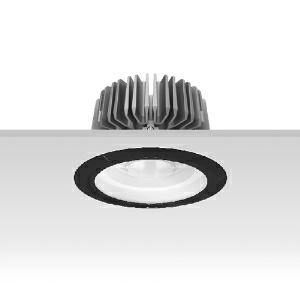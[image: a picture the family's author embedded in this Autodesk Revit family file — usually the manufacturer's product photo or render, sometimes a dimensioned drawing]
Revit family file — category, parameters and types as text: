
# Revit family: 3f_filippi_-_3f_reno_bianco_ampio_3f_filippi_-_30387_a01024_-_3f_reno_150_wh_3000-930_dali_wide___vt_bk_413a
name_source: partatom
category: Lighting Fixtures
units: mm (PartAtom-declared; Revit-internal decimal feet)

## family parameters
Cut with Voids When Loaded = No
Host = Face
Light Source = No
Part Type = Normal
Room Calculation Point = No
Round Connector Dimension = Use Diameter
Shared = No

## types (1)
- 3F Filippi - 3F Reno Bianco Ampio (1 x LED, 2656 lm, 37 W, 3000 K)
    Apparent Load = 37 VA
    Approval mark = CE
    CIE Flux Codes = 74 93 99 100 100
    Color Rendering = 90
    Color Temperature = 3000 K
    Control Gear = Electronic transformer
    Default Elevation = 1800 mm
    Description = ILLUMINOTECHNICAL
Luminous efficiency 100% (DLOR 100%, ULOR 0%).
Initial luminous flux of the luminaire 2656 lm.
Direct symmetric wide distribution.
Installation Interdistance Transv.D = 1.54 x hu - Long.D = 1.54 x hu.
Tabular UGR (CIE 117 - 4H-8H; S=0.25H; 70/50/20): RUG 24.4 - 24.2.
Beam angle: 74° - 73°.
Luminous efficacy 72 lm/W.
Lifetime (L90/B10): 30000 h. (tq+25°C)
Lifetime (L85/B10): 50000 h. (tq+25°C)
Lifetime (L70/B10): 80000 h. (tq+25°C)
Sudden decreased luminous flux after 50000 hours: 0% (C0).
Photobiological safety in compliance with IEC/TR 62778: RG0 risk exempt, (IEC 62471).
In compliance with IEC/EN 62722-2-1 - IEC/EN 62717 standards.

SOURCE
Compact LED module 3000/930.
Energy efficiency class (UE 2019/2020 - UE 2019/2015): F.
CIE 13.3 Colour rendering index: CRI >90 (R9 >50%).
IES TM-30 Fidelity Index: Rf = 92 Rg = 101.
CCT nominal colour temperature 3000 K.
Colour initial tolerance (MacAdam): SDCM 3.
Zhaga Book 3 compliant.

MECHANICAL
Passive heat dissipator in die-casting aluminium, oversized, for optimum thermal management of the LED module.
Parabolic element with graduated/concentric rings in white polycarbonate.
Transparent external lens with glossy and satin differentiated surfaces, with a cooling and anti-insect system in methacrylate (PMMA).
Fastening spring clips in stainless steel.
Dimensions: diameter 176 mm, height 111 mm. Weight 1.51 kg.
IP44 protection degree for exposed part, IP20 for recessed part.
Mechanical strength to impacts IK06 (1 joule).
Glow-wire test resistance 650°C.

ELECTRICAL
Wiring on a separate unit.
Halogen Free DALI-2 DATI (Parts 251, 252, 253), PUSH-DIM, electronic wiring 230V-50/60Hz, power factor 0.97 at full load, THD <25%, constant output current, SELV, class II, 1 driver, 1 DALI addresse.
Power of the luminaire 37 W.
ENEC - CE.
SAFE FLICKER: PstLM=<1 and SVM=<0.4 (IEC TR 61547-1 and IEC TR 63158), to ensure a more comfortable and safe light.
Luminaire compliant with EN 60598-2-22 for power supply from a centralised emergency system CPSS (Central Power Supply System), not incorporated in the luminaire - high risk areas excluded. The default power and flux are 100% in AC and 100% in DC.
Ambient temperature from 0°C to +25°C.
Temperature class T6 max 85°C.
Relative humidity UR: <85%.

INSTALLATION
Pull-up recessed fitting.
False ceiling carving: 150 mm.
All accessories dedicated to this product are available on the Catalog and on our website www.3F-Filippi.com.

ACCESSORIES
A01024 - VT transparent glass, tempered, not flammable, locked and in line with the trim, in black polycarbonate.

APPLICATIONS
Environments: architectural, commercial, exhibition areas, transit areas, corridors, shops, display windows, service areas.
In false ceilings with narrow voids.

LIGHT MANAGEMENT
Recommended minimum setting: 10%.
The luminaire, equipped with (DALI-2 DATI) driver, can be controlled manually with 3F Easy Dim technology or automatically/manually with wired or wireless DALI/D2D control systems.
The D2D driver guarantees interoperability with other devices with the same certification by making the following information available:
Device Data (Part 251), Energy Report (Part 252), Diagnosis & Maintenance (Part 253).
In electrical systems without a regulation system (manual or automatic) and DALI bus, a suitable jumper must be made on the DA-DA terminals of the appliance.

WARNING
Luminaire designed for disposal/recycling at end-of-life.
Replaceable (LED only) light source by a professional. Replaceable control gear by a professional.
    Height = 0 mm  [stored 0 ft]
    Lamp = 1 x LED
    Lamp Light Flux = 2656 lm
    Lamp Power = 37 W
    Lamp count = 1
    Length = 176 mm
    Lifetime = 50000 h
    Luminous efficacy = 72 lm/W
    Manufacturer = 3F Filippi
    ModVariant = No
    Model = 3F Filippi - 30387+A01024 - 3F Reno 150 WH 3000-930 DALI WIDE + VT BK
    Mounting Place = Ceiling
    Mounting Type = Recessed
    Number of Poles = 1
    OnlyDefault = Yes
    Power Factor = 1
    Product Name = 3F Filippi - 3F Reno Bianco Ampio
    Product group = recessed luminaire
    ProductGroupID = 4
    Protection Class = Protection class II
    Protection Degree = IP 20
    RLX_Detail_Level = 1
    RLX_Emergency_Light_Flux = 0 lm
    RLX_Emergency_Type = 0
    RLX_Emergency_Type_DB = No
    RlxData = <blob elided: 90469 chars, md5=4c992c80>
    Socket = socket
    Standby Power = 0 W
    System Light Flux = 2656 lm
    System Power = 37 W
    Type Comments = Product without accessories
    Type Image = 3ffilippi_3f_reno_150_wh_d150__a01024.jpg
    URL = http://relux.com
    VarID = ---
    Voltage = 0 V
    Weight = 0.00 kg
    Width = 0 mm  [stored 0 ft]

note: [stored X ft] marks values corroborated as IEEE doubles in the binary element streams (Revit-internal decimal feet)

## geometry (parser evidence)
native form markers: Blend x4, Sweep x12
no freeform markers — native parametric forms only
